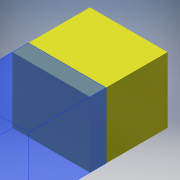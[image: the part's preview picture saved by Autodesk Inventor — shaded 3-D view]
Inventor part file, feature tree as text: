
AUTODESK INVENTOR PART (.ipt)
format: ipt  version: 2017 SP1 (Build 210196100, 196)  size: 85,504 bytes
history: native  units: in
note: dims shown in document units (in); Inventor stores cm internally (conversion verified against a paired STEP export)
features: extrude x1, sketch x1
ambient origin geometry x8: Origin, YZ Plane, XZ Plane, XY Plane, X Axis, Y Axis, Z Axis, Center Point
bodies: Solid1 (feature_tree)
feature tree (2):
  extrude  "Extrusion1"  Depth=11.0in TaperAngle=0.0deg
  sketch  "Sketch1"  dims[d0=13.0in d1=11.0in d2=0.0in]
